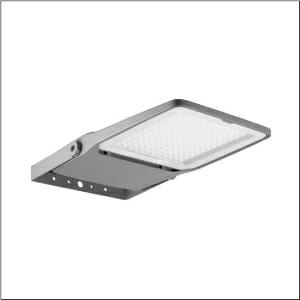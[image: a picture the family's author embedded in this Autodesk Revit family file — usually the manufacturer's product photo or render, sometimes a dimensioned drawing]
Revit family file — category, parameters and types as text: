
# Revit family: floodlight_fl_20_midi___pl52_5xa7682e3d2ac_2b6a
name_source: partatom
category: Lighting Fixtures
units: mm (PartAtom-declared; Revit-internal decimal feet)

## family parameters
Cut with Voids When Loaded = No
Host = Face
Light Source = No
Part Type = Normal
Room Calculation Point = No
Round Connector Dimension = Use Diameter
Shared = No

## types (1)
- --- (1 x LED 5000K / CRI = 70 (unbekannt), 27250 lm, 5000K)
    Apparent Load = 208 VA
    CIE Flux Codes = 27 59 98 100 100
    Color Rendering = 70
    Color Temperature = 5000K
    Default Elevation = 1800 mm
    Description = Floodlight FL 20 midi, floodlight, primary light control with lens, of plastic, primary optical cover: protective disc, of toughened safety glass, transparent, light distribution: PL52, light emission: direct distribution, primary light characteristic: asymmetric, installation type: surface-mounted, LED, High Power LED, rated luminous flux: 27.250lm, luminous efficacy: 131lm/W, light colour: 750, colour temperature: 5000K, control gear: ECG Plus, control: flexible luminous flux parameterisation, time-dependent luminous flux control, digital communication interface, power reduction, overheat protection, electronic power reduction, with terminal, 5-pole, max. 2.5mm², mains connection: 220..240V, AC, 50/60Hz, rated input power: 208W, LED unit, of diecast aluminium, powder-coated, Siteco® metallic grey (DB 702S), corrosivity category C5 mid according to DIN EN ISO 12944, incl. 1x M20 cable gland for cable Ø 6.5..12mm, length: 731mm, width: 450mm, height: 76mm, housing frame, of diecast aluminium, powder-coated, Siteco® metallic grey (DB 702S), wall fastening, of steel, powder-coated, Siteco® metallic grey (DB 702S), DALI, protection rating (complete): IP66, insulation class (complete): insulation class II (safety insulation), certification: CE, ENEC, VDE, protection symbol: D, permissible operating ambient temperature: -40..+40°C, permissible operating ambient temperature for outdoor applications: -40..+50°C, standard: DIN EN 12944, packaging unit: 1 piece

Light Distribution: PL52
    Height = 76 mm
    Lamp = 1 x LED 5000K / CRI >= 70 (unbekannt)
    Lamp Light Flux = 27250 lm
    Lamp count = 1
    Length = 731 mm
    Luminous efficacy = 131 lm/W
    Manufacturer = Siteco
    ModVariant = No
    Model = 5XA7682E3D2AC
    Mounting Place = Wall
    Mounting Type = Surface mounted
    Number of Poles = 1
    OnlyDefault = Yes
    Power Factor = 1
    Product Name = Floodlight FL 20 midi | PL52
    Product group = floodlight | wall mounted
    ProductGroupID = 2001
    Protection Class = Protection class II
    Protection Degree = IP 66
    RLX_Detail_Level = 1
    RLX_Emergency_Light_Flux = 0 lm
    RLX_Emergency_Type = 0
    RLX_Emergency_Type_DB = No
    RlxData = <blob elided: 92489 chars, md5=a425ae3a>
    Socket = socket
    Standby Power = 0 W
    System Light Flux = 27250 lm
    System Power = 208 W
    Type Comments = factory setting: luminous flux: 100 % | dim-lin: 254 | 484 mA
    Type Image = l_1005944.jpg
    URL = http://relux.com
    VarID = @adj_147461
    Voltage = 0 V
    Weight = 0.00 kg
    Width = 450 mm

## geometry (parser evidence)
native form markers: Blend x4, Sweep x15
no freeform markers — native parametric forms only
